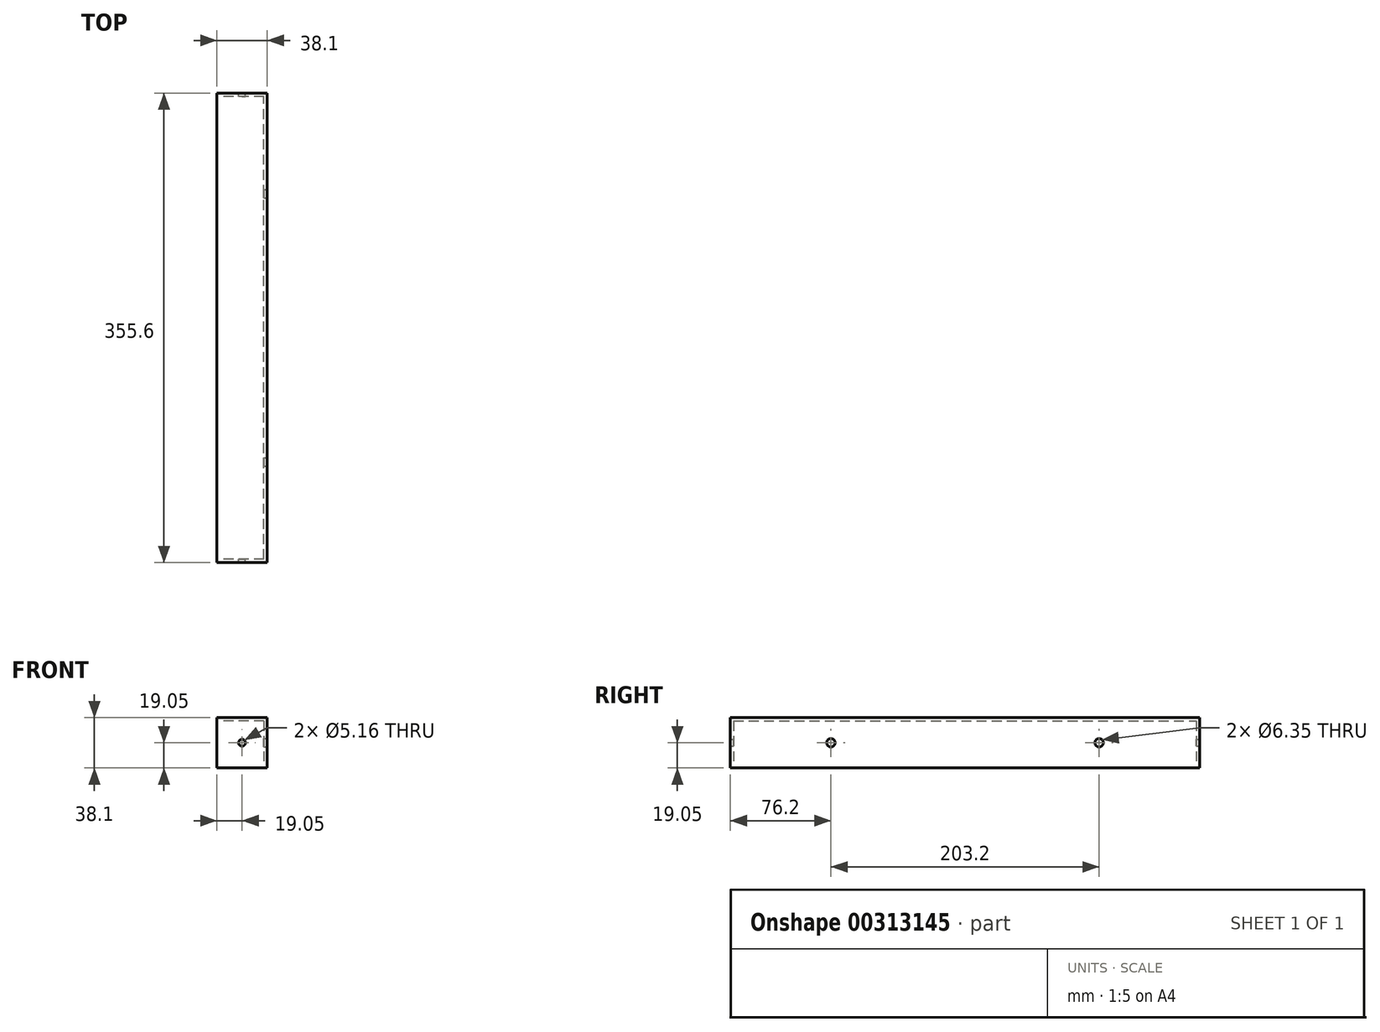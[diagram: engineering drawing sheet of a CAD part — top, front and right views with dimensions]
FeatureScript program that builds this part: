
annotation { "Feature Type Name" : "Feature", "Feature Type Description" : "" }
export const myFeature = defineFeature(function(context is Context, id is Id, definition is map)
    precondition{}
    {
        {
            var Q0;
            Q0=qCreatedBy(makeId("Front.planeOp"),FACE);
            var sketch = newSketch(context, id + "F0", { "sketchPlane" : qUnion([Q0])});
            skLineSegment(sketch, "E0.bottom", {"start": v(19.05, 19.05) * mm, "end": v(-19.05, 19.05) * mm});
            skLineSegment(sketch, "E0.top", {"start": v(19.05, -19.05) * mm, "end": v(-19.05, -19.05) * mm});
            skLineSegment(sketch, "E0.left", {"start": v(19.05, 19.05) * mm, "end": v(19.05, -19.05) * mm});
            skLineSegment(sketch, "E0.right", {"start": v(-19.05, 19.05) * mm, "end": v(-19.05, -19.05) * mm});
            skPoint(sketch, "E0.middle", {"position": v(0, 0) * mm});
            skSolve(sketch);
        }
        {
            var Q0;
            Q0=qSketchRegion(id+"F0",true);
            extrude(context, id + "F1", {"entities" : qUnion([Q0]), "endBound" : BoundingType.SYMMETRIC, "depth" : 355.6 * mm, "offsetDistance" : 25.4 * mm});
        }
        {
            var Q0;
            Q0=makeQuery(id+"F1.opExtrude","SWEPT_FACE",FACE,{"disambiguationData":[OSD([sQuery(id+"F0.wireOp",EDGE,"E0.right")])]});
            var Q1;
            Q1=makeQuery(id+"F1.opExtrude","SWEPT_FACE",FACE,{"disambiguationData":[OSD([sQuery(id+"F0.wireOp",EDGE,"E0.top")])]});
            shell(context, id + "F2", {"entities" : qUnion([Q0, Q1]), "thickness" : 2.54 * mm});
        }
        {
            var Q0;
            Q0=makeQuery(id+"F1.opExtrude","CAP_FACE",FACE,{"disambiguationData":[OSD([sQuery(id+"F0.wireOp",EDGE,"E0.bottom"),sQuery(id+"F0.wireOp",EDGE,"E0.top"),sQuery(id+"F0.wireOp",EDGE,"E0.left"),sQuery(id+"F0.wireOp",EDGE,"E0.right")])],"isStart":true});
            var sketch = newSketch(context, id + "F3", { "sketchPlane" : qUnion([Q0])});
            skCircle(sketch, "E1", {"center": v(0, 0) * mm, "radius": 2.58 * mm});
            skPoint(sketch, "E1.centerSnap0", {"position": v(-19.05, 0) * mm});
            skPoint(sketch, "E1.centerSnap1", {"position": v(0, 19.05) * mm});
            skSolve(sketch);
        }
        {
            var Q0;
            Q0 = qSketchRegion(id + "F3", true);
            extrude(context, id + "F4", {"entities" : qUnion([Q0]), "operationType" : NewBodyOperationType.REMOVE, "endBound" : BoundingType.THROUGH_ALL, "oppositeDirection" : true, "depth" : 25.4 * mm});
        }
        {
            var Q0;
            Q0=makeQuery(id+"F1.opExtrude","SWEPT_FACE",FACE,{"disambiguationData":[OSD([sQuery(id+"F0.wireOp",EDGE,"E0.left")])]});
            var sketch = newSketch(context, id + "F5", { "sketchPlane" : qUnion([Q0])});
            skCircle(sketch, "E2", {"center": v(-101.6, 0) * mm, "radius": 3.18 * mm});
            skPoint(sketch, "E2.centerSnap0", {"position": v(-177.8, 0) * mm});
            skCircle(sketch, "E3", {"center": v(101.6, 0) * mm, "radius": 3.18 * mm});
            skSolve(sketch);
        }
        {
            var Q0;
            Q0 = qSketchRegion(id + "F5", true);
            extrude(context, id + "F6", {"entities" : qUnion([Q0]), "operationType" : NewBodyOperationType.REMOVE, "endBound" : BoundingType.THROUGH_ALL, "oppositeDirection" : true, "depth" : 25.4 * mm});
        }
    });
